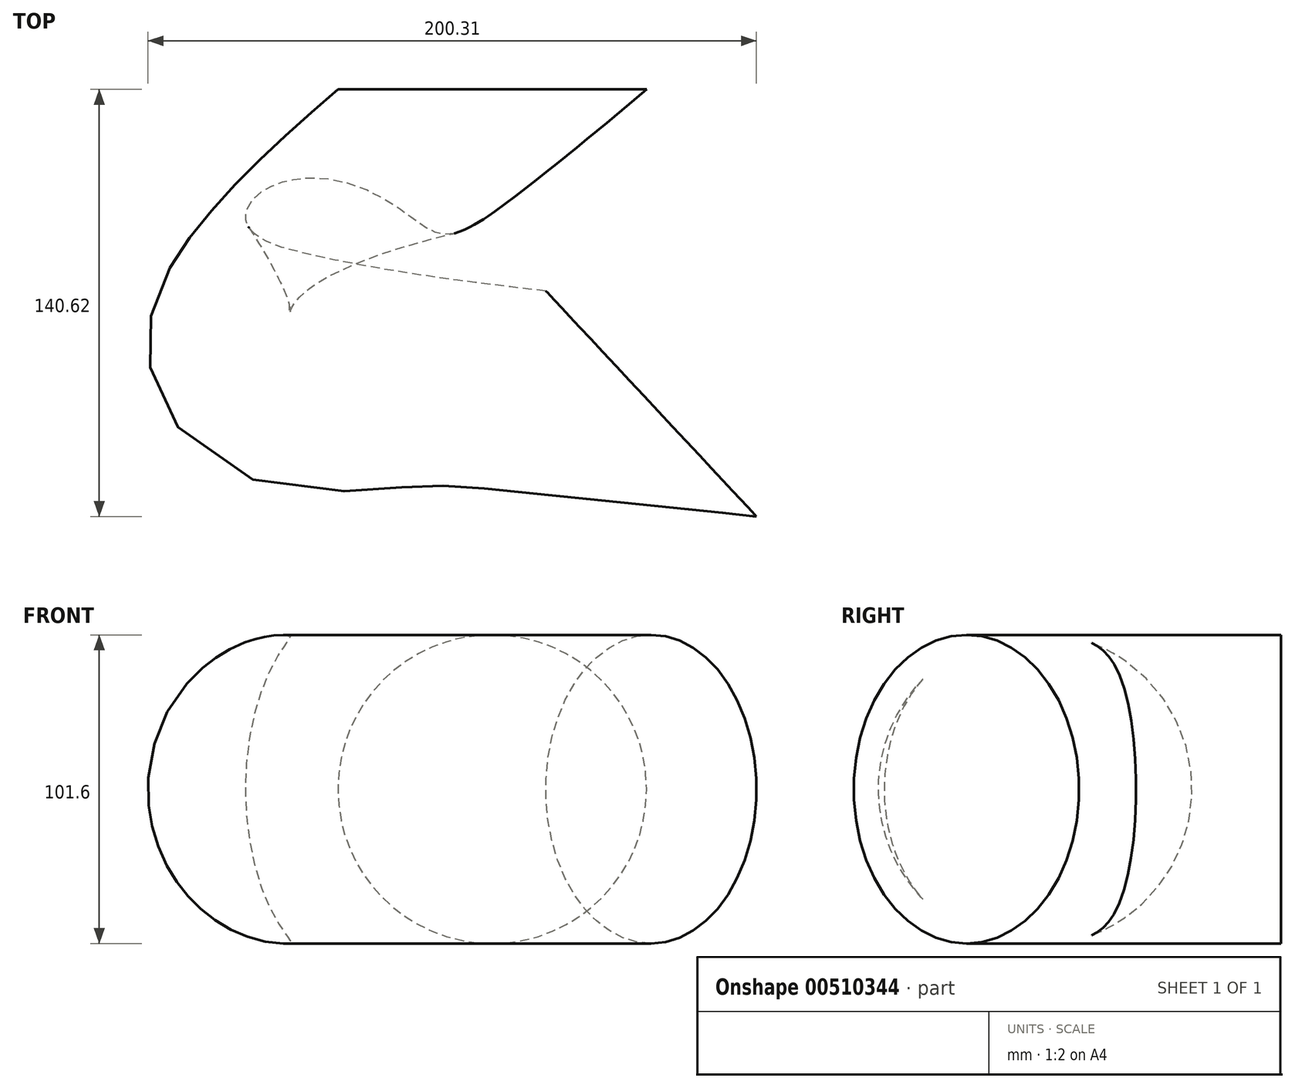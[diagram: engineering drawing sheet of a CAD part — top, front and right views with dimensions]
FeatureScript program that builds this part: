
annotation { "Feature Type Name" : "Feature", "Feature Type Description" : "" }
export const myFeature = defineFeature(function(context is Context, id is Id, definition is map)
    precondition{}
    {
        {
            var Q0;
            Q0=qCreatedBy(makeId("Front.planeOp"),FACE);
            var sketch = newSketch(context, id + "F0", { "sketchPlane" : qUnion([Q0])});
            skCircle(sketch, "E0", {"center": v(0, 0) * mm, "radius": 50.8 * mm});
            skSolve(sketch);
        }
        {
            var Q0;
            Q0=qCreatedBy(makeId("Top.planeOp"),FACE);
            var sketch = newSketch(context, id + "F1", { "sketchPlane" : qUnion([Q0])});
            skFitSpline(sketch, "E1", {"points": [v(0, 0) * mm, v(-68.67, -76.12) * mm, v(-34.86, -92) * mm, v(52.3, -103.49) * mm], "startDerivative": vector(-269.67, -231.14) * mm, "endDerivative": vector(249.74, -27.83) * mm});
            skSolve(sketch);
        }
        {
            var Q0;
            Q0=makeQuery(id+"F0.imprint","IMPRINT",FACE,{"disambiguationData":[TD([[makeQuery(id+"F0.imprint","IMPRINT",EDGE,{"derivedFrom":sQuery(id+"F0.wireOp",EDGE,"E0")}),1.0]])]});
            var Q1;
            Q1=sQuery(id+"F1.wireOp",EDGE,"E1");
            sweep(context, id + "F2", {"profiles" : qUnion([Q0]), "path" : qUnion([Q1])});
        }
    });
